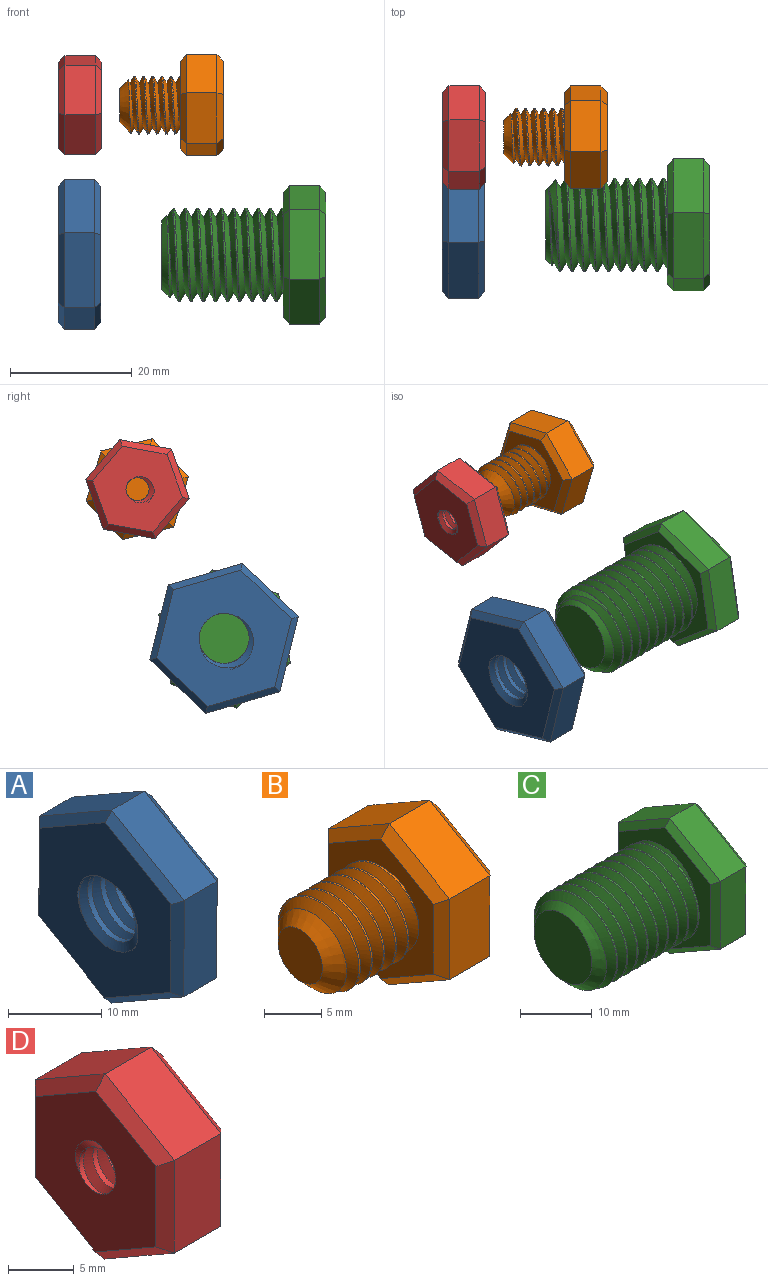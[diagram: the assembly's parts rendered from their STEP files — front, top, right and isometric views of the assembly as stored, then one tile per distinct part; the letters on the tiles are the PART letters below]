
ASSEMBLY  parts=4 mates=2
PART A: 23 faces, bbox 9.3x22.6x26 mm
  f0: cylinder r=4.12mm len=8.24mm, axis (1,0,0), area 63.5mm2, adj f7,f8,f21,f22
  f1: plane 10.98x6.38mm, normal (0,-0.5,0.86), area 63.5mm2, adj f2,f6,f14,f18
  f2: plane 12.7x5mm, normal (0,-1,0), area 63.5mm2, adj f1,f3,f12,f16
  f3: plane 11.02x6.32mm, normal (0,-0.5,-0.87), area 63.5mm2, adj f2,f4,f10,f15
  f4: plane 10.98x6.38mm, normal (0,0.5,-0.86), area 63.5mm2, adj f3,f5,f9,f17
  f5: plane 12.7x5mm, normal (0,1,0), area 63.5mm2, adj f4,f6,f11,f19
  f6: plane 11.02x6.32mm, normal (0,0.5,0.87), area 63.5mm2, adj f1,f5,f13,f20
  f7: plane 23.7x20.63mm, normal (-1,0,0), area 282.8mm2, adj f0,f9,f10,f11,f12,f13,f14,f21
  f8: plane 23.7x20.63mm, normal (1,0,0), area 282.8mm2, adj f0,f15,f16,f17,f18,f19,f20,f21
  f9: plane 10.99x6.96mm, normal (-0.71,0.36,-0.61), area 17.1mm2, adj f4,f7,f10,f11
  f10: plane 11.02x6.9mm, normal (-0.71,-0.35,-0.61), area 17.1mm2, adj f3,f7,f9,f12
  f11: plane 12.7x1.03mm, normal (-0.71,0.71,0), area 17.1mm2, adj f5,f7,f9,f13
  f12: plane 12.7x1.03mm, normal (-0.71,-0.71,0), area 17.1mm2, adj f2,f7,f10,f14
  f13: plane 11.02x6.9mm, normal (-0.71,0.35,0.61), area 17.1mm2, adj f6,f7,f11,f14
  f14: plane 10.99x6.96mm, normal (-0.71,-0.36,0.61), area 17.1mm2, adj f1,f7,f12,f13
  f15: plane 11.02x6.9mm, normal (0.71,-0.35,-0.61), area 17.1mm2, adj f3,f8,f16,f17
  f16: plane 12.7x1.03mm, normal (0.71,-0.71,0), area 17.1mm2, adj f2,f8,f15,f18
  f17: plane 10.99x6.96mm, normal (0.71,0.36,-0.61), area 17.1mm2, adj f4,f8,f15,f19
  f18: plane 10.99x6.96mm, normal (0.71,-0.36,0.61), area 17.1mm2, adj f1,f8,f16,f20
  f19: plane 12.7x1.03mm, normal (0.71,0.71,0), area 17.1mm2, adj f5,f8,f17,f20
  f20: plane 11.02x6.9mm, normal (0.71,0.35,0.61), area 17.1mm2, adj f6,f8,f18,f19
  f21: bspline ~12.11x10.49mm, area 133.9mm2, adj f0,f7,f8,f22
  f22: bspline ~12.11x10.49mm, area 133.9mm2, adj f0,f7,f8,f21
PART B: 25 faces, bbox 17.8x15.9x18.1 mm
  f0: cylinder r=4.75mm len=9.5mm, axis (1,0,0), area 28.1mm2, adj f1,f2,f4,f12
  f1: bspline ~10.97x9.91mm, area 196.7mm2, adj f0,f2,f4,f12
  f2: bspline ~10.97x10.66mm, area 196.6mm2, adj f0,f1,f4,f12
  f3: plane 5.5x5.5mm, normal (-1,0,0), area 23.8mm2, adj f4
  f4: cone r=4.75mm half-angle=45deg, axis (1,0,0), area 47.4mm2, adj f0,f1,f2,f3
  f5: plane 7.48x5mm, normal (0,-0.5,0.86), area 43.3mm2, adj f6,f10,f18,f22
  f6: plane 8.66x5mm, normal (0,-1,0), area 43.3mm2, adj f5,f7,f16,f20
  f7: plane 7.52x5mm, normal (0,-0.5,-0.87), area 43.3mm2, adj f6,f8,f14,f19
  f8: plane 7.48x5mm, normal (0,0.5,-0.86), area 43.3mm2, adj f7,f9,f13,f21
  f9: plane 8.66x5mm, normal (0,1,0), area 43.3mm2, adj f8,f10,f15,f23
  f10: plane 7.52x5mm, normal (0,0.5,0.87), area 43.3mm2, adj f5,f9,f17,f24
  f11: plane 15.01x13.03mm, normal (1,0,0), area 146.4mm2, adj f13,f14,f15,f16,f17,f18
  f12: plane 15.83x13.85mm, normal (-1,0,0), area 89.2mm2, adj f0,f1,f2,f19,f20,f21,f22,f23
  f13: plane 7.49x4.93mm, normal (0.71,0.36,-0.61), area 11.4mm2, adj f8,f11,f14,f15
  f14: plane 7.52x4.88mm, normal (0.71,-0.35,-0.61), area 11.4mm2, adj f7,f11,f13,f16
  f15: plane 8.66x1.03mm, normal (0.71,0.71,0), area 11.4mm2, adj f9,f11,f13,f17
  f16: plane 8.66x1.03mm, normal (0.71,-0.71,0), area 11.4mm2, adj f6,f11,f14,f18
  f17: plane 7.52x4.88mm, normal (0.71,0.35,0.61), area 11.4mm2, adj f10,f11,f15,f18
  f18: plane 7.49x4.93mm, normal (0.71,-0.36,0.61), area 11.4mm2, adj f5,f11,f16,f17
  f19: plane 7.52x4.88mm, normal (-0.71,-0.35,-0.61), area 11.4mm2, adj f7,f12,f20,f21
  f20: plane 8.66x1.03mm, normal (-0.71,-0.71,0), area 11.4mm2, adj f6,f12,f19,f22
  f21: plane 7.49x4.93mm, normal (-0.71,0.36,-0.61), area 11.4mm2, adj f8,f12,f19,f23
  f22: plane 7.49x4.93mm, normal (-0.71,-0.36,0.61), area 11.4mm2, adj f5,f12,f20,f24
  f23: plane 8.66x1.03mm, normal (-0.71,0.71,0), area 11.4mm2, adj f9,f12,f21,f24
  f24: plane 7.52x4.88mm, normal (-0.71,0.35,0.61), area 11.4mm2, adj f10,f12,f22,f23
PART C: 26 faces, bbox 27.7x20x23.1 mm
  f0: cylinder r=7.68mm len=18mm, axis (1,0,0), area 139.1mm2, adj f1,f2,f5,f13
  f1: bspline ~20.88x17.74mm, area 713.8mm2, adj f0,f2,f4,f5,f13
  f2: bspline ~21.88x17.74mm, area 715.1mm2, adj f0,f1,f4,f5,f13
  f3: plane 11.36x11.36mm, normal (-1,0,0), area 101.4mm2, adj f4
  f4: cone r=7.68mm half-angle=45deg, axis (1,0,0), area 63.2mm2, adj f1,f2,f3,f5
  f5: cone r=7.68mm half-angle=45deg, axis (1,0,0), area 13.2mm2, adj f0,f1,f2,f4
  f6: plane 9.98x5.81mm, normal (0,-0.5,0.86), area 57.7mm2, adj f7,f11,f19,f23
  f7: plane 11.55x5mm, normal (0,-1,0), area 57.7mm2, adj f6,f8,f17,f21
  f8: plane 10.02x5.74mm, normal (0,-0.5,-0.87), area 57.7mm2, adj f7,f9,f15,f20
  f9: plane 9.98x5.81mm, normal (0,0.5,-0.86), area 57.7mm2, adj f8,f10,f14,f22
  f10: plane 11.55x5mm, normal (0,1,0), area 57.7mm2, adj f9,f11,f16,f24
  f11: plane 10.02x5.74mm, normal (0,0.5,0.87), area 57.7mm2, adj f6,f10,f18,f25
  f12: plane 20.78x18.04mm, normal (1,0,0), area 280.6mm2, adj f14,f15,f16,f17,f18,f19
  f13: plane 20.78x18.04mm, normal (-1,0,0), area 125.2mm2, adj f0,f1,f2,f20,f21,f22,f23,f24
  f14: plane 9.98x6.38mm, normal (0.71,0.36,-0.61), area 15.5mm2, adj f9,f12,f15,f16
  f15: plane 10.02x6.32mm, normal (0.71,-0.35,-0.61), area 15.5mm2, adj f8,f12,f14,f17
  f16: plane 11.55x1.04mm, normal (0.71,0.71,0), area 15.5mm2, adj f10,f12,f14,f18
  f17: plane 11.55x1.04mm, normal (0.71,-0.71,0), area 15.5mm2, adj f7,f12,f15,f19
  f18: plane 10.02x6.32mm, normal (0.71,0.35,0.61), area 15.5mm2, adj f11,f12,f16,f19
  f19: plane 9.98x6.38mm, normal (0.71,-0.36,0.61), area 15.5mm2, adj f6,f12,f17,f18
  f20: plane 10.02x6.32mm, normal (-0.71,-0.35,-0.61), area 15.5mm2, adj f8,f13,f21,f22
  f21: plane 11.55x1.04mm, normal (-0.71,-0.71,0), area 15.5mm2, adj f7,f13,f20,f23
  f22: plane 9.98x6.38mm, normal (-0.71,0.36,-0.61), area 15.5mm2, adj f9,f13,f20,f24
  f23: plane 9.98x6.38mm, normal (-0.71,-0.36,0.61), area 15.5mm2, adj f6,f13,f21,f25
  f24: plane 11.55x1.04mm, normal (-0.71,0.71,0), area 15.5mm2, adj f10,f13,f22,f25
  f25: plane 10.02x6.32mm, normal (-0.71,0.35,0.61), area 15.5mm2, adj f11,f13,f23,f24
PART D: 23 faces, bbox 9.2x15.5x17.8 mm
  f0: cylinder r=1.9mm len=7mm, axis (1,0,0), area 26.8mm2, adj f7,f8,f21,f22
  f1: plane 7.49x5mm, normal (0,-0.5,0.86), area 43.3mm2, adj f2,f6,f14,f18
  f2: plane 8.66x5mm, normal (0,-1,0), area 43.3mm2, adj f1,f3,f12,f16
  f3: plane 7.51x5mm, normal (0,-0.5,-0.87), area 43.3mm2, adj f2,f4,f10,f15
  f4: plane 7.49x5mm, normal (0,0.5,-0.86), area 43.3mm2, adj f3,f5,f9,f17
  f5: plane 8.66x5mm, normal (0,1,0), area 43.3mm2, adj f4,f6,f11,f19
  f6: plane 7.51x5mm, normal (0,0.5,0.87), area 43.3mm2, adj f1,f5,f13,f20
  f7: plane 15.5x13.51mm, normal (-1,0,0), area 130.8mm2, adj f0,f9,f10,f11,f12,f13,f14,f21
  f8: plane 15.5x13.51mm, normal (1,0,0), area 130.8mm2, adj f0,f15,f16,f17,f18,f19,f20,f21
  f9: plane 7.49x4.93mm, normal (-0.71,0.36,-0.61), area 11.4mm2, adj f4,f7,f10,f11
  f10: plane 7.51x4.89mm, normal (-0.71,-0.35,-0.61), area 11.4mm2, adj f3,f7,f9,f12
  f11: plane 8.66x1.02mm, normal (-0.71,0.71,0), area 11.4mm2, adj f5,f7,f9,f13
  f12: plane 8.66x1.02mm, normal (-0.71,-0.71,0), area 11.4mm2, adj f2,f7,f10,f14
  f13: plane 7.51x4.89mm, normal (-0.71,0.35,0.61), area 11.4mm2, adj f6,f7,f11,f14
  f14: plane 7.49x4.93mm, normal (-0.71,-0.36,0.61), area 11.4mm2, adj f1,f7,f12,f13
  f15: plane 7.51x4.89mm, normal (0.71,-0.35,-0.61), area 11.4mm2, adj f3,f8,f16,f17
  f16: plane 8.66x1.02mm, normal (0.71,-0.71,0), area 11.4mm2, adj f2,f8,f15,f18
  f17: plane 7.49x4.93mm, normal (0.71,0.36,-0.61), area 11.4mm2, adj f4,f8,f15,f19
  f18: plane 7.49x4.93mm, normal (0.71,-0.36,0.61), area 11.4mm2, adj f1,f8,f16,f20
  f19: plane 8.66x1.02mm, normal (0.71,0.71,0), area 11.4mm2, adj f5,f8,f17,f20
  f20: plane 7.51x4.89mm, normal (0.71,0.35,0.61), area 11.4mm2, adj f6,f8,f18,f19
  f21: bspline ~8.75x6.44mm, area 70.5mm2, adj f0,f7,f8,f22
  f22: bspline ~8.5x6.44mm, area 70.5mm2, adj f0,f7,f8,f21
PLACE A rot(axis=(0,0.6,-0.8),180deg) t=(-55.27,-6.86,23.48)mm fixed
PLACE B rot(axis=(-1,0,0),43.8deg) t=(-31.66,7.43,48.03)mm
PLACE C rot(axis=(1,0,0),109.9deg) t=(-14.77,-6.94,23.4)mm
PLACE D rot(axis=(1,0,0),100.2deg) t=(-48.16,7.38,48.02)mm fixed
MATE cylindrical C.f0 <-> A.f7  axis (-1,0,0) through (-38.27,-6.94,23.4)mm
MATE cylindrical B.f0 <-> D.f7  axis (-1,0,0) through (-45.16,7.43,48.03)mm
